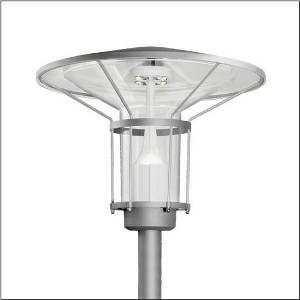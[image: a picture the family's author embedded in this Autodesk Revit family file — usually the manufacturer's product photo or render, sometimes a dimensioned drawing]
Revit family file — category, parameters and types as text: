
# Revit family: laterne_classic_iq___st1_2a_5xa5245af14h_9f1a
name_source: partatom
category: Lighting Fixtures
units: mm (PartAtom-declared; Revit-internal decimal feet)

## family parameters
Cut with Voids When Loaded = No
Host = Face
Light Source = No
Part Type = Normal
Room Calculation Point = No
Round Connector Dimension = Use Diameter
Shared = No

## types (1)
- --- (1 x LED, 1380 lm, 12.9 W, 2200K)
    Apparent Load = 13 VA
    CIE Flux Codes = 21 60 93 97 100
    Color Rendering = 70
    Color Temperature = 2200K
    Default Elevation = 1800 mm
    Description = Lantern Classic iQ, mast luminaire, Module 540 iQ-SR, primary light control with 3 zone facetted reflector, of plastic, silver coated, highly specular, structured, primary optical cover: cover, of PMMA, transparent, light distribution: ST1.2a, light emission: direct distribution, primary light characteristic: asymmetric, installation type: post-top, LED, High Power LED, rated luminous flux: 1.380lm, luminous efficacy: 107lm/W, light colour: 722, colour temperature: 2200K, control gear: ECG iQ, control: presetting dimming logarithmic, Street-Remote, Auto-Match, Temp-Guard, Lumen-Switch, Night-Set, Smart-Wire, Light-Fading, Desk-Remote (wireless, voltage-free reading and setting of iQ features in the workshop via application-optimized NFC function/RFID function), optimised constant luminous flux control (CLO 2.0), with terminal, 6-pole, max. 2.5mm², mains connection: 220..240V, AC, 50/60Hz, start of lifetime: 13W, end of lifetime: 13W, reduction: 6W, luminaire housing, upper part, of glass-fibre reinforced polyester, coated, Siteco® metallic grey (DB 702S), diameter: 750mm, height: 596mm, spigot size: d x l = 76 x 70mm (post-top) | with reducer (optional accessory) 60 x 70mm, post-top mast mounting element, of diecast aluminium, coated, Siteco® metallic grey (DB 702S), Module 540 iQ-SR, traffic white (RAL 9016), equipment: standard, protection rating (complete): IP65, insulation class (complete): insulation class II (safety insulation), certification: CE, ENEC, VDE, packaging unit: 1 piece

Light Distribution: ST1.2a
    Height = 596 mm
    Lamp = 1 x LED
    Lamp Light Flux = 1380 lm
    Lamp Power = 12.9 W
    Lamp count = 1
    Length = 750 mm
    Luminous efficacy = 107 lm/W
    Manufacturer = Siteco
    ModVariant = No
    Model = 5XA5245AF14H
    Number of Poles = 1
    OnlyDefault = Yes
    Power Factor = 1
    Product Name = Laterne Classic iQ | ST1.2a
    Product group = mast luminaire | pylon top
    ProductGroupID = 6100
    Protection Class = Protection class II
    Protection Degree = IP 65
    RLX_Detail_Level = 1
    RlxData = <blob elided: 92069 chars, md5=4bbf3498>
    Socket = socket
    Standby Power = 0 W
    System Light Flux = 1380 lm
    System Power = 13 W
    Type Comments = factory setting: luminous flux: 100 % | dim-lin: 254 | 516 mA
    Type Image = l_1006052.jpg
    URL = http://relux.com
    VarID = @adj_071653
    Voltage = 0 V
    Weight = 0.00 kg
    Width = 0 mm  [stored 0 ft]

note: [stored X ft] marks values corroborated as IEEE doubles in the binary element streams (Revit-internal decimal feet)

## geometry (parser evidence)
native form markers: Blend x4, Sweep x14
no freeform markers — native parametric forms only
